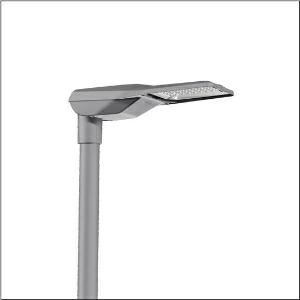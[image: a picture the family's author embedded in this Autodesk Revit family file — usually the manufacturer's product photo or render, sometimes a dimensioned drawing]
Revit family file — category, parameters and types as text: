
# Revit family: streetlight_sl_21_iq_mini___st0_8a_5xe2c41d08gb_f485
name_source: partatom
category: Lighting Fixtures
units: mm (PartAtom-declared; Revit-internal decimal feet)

## family parameters
Cut with Voids When Loaded = No
Host = Face
Light Source = No
Part Type = Normal
Room Calculation Point = No
Round Connector Dimension = Use Diameter
Shared = No

## types (1)
- --- (1 x LED, 5920 lm, 37.1 W, 4000K)
    Apparent Load = 37 VA
    CIE Flux Codes = 38 75 97 100 100
    Color Rendering = 70
    Color Temperature = 4000K
    Default Elevation = 1800 mm
    Description = Streetlight SL 21 iQ mini, mast luminaire, primary light control with lens, of PMMA, primary optical cover: cover, of toughened safety glass, transparent, light distribution: ST0.8a, light emission: direct distribution, primary light characteristic: asymmetric, installation type: post-top, side-entry, LED, High Power LED, rated luminous flux: 5.920lm, luminous efficacy: 160lm/W, light colour: 740, colour temperature: 4000K, control: Auto-Match, Temp-Guard, Lumen-Switch, Night-Set, Smart-Wire, Light-Fading, Desk-Remote (wireless, voltage-free reading and setting of iQ features in the workshop via application-optimized NFC function/RFID function), optimised constant luminous flux control (CLO 2.0), presetting dimming linear, mains connection: 220..240V, AC, 50/60Hz, start of lifetime: 37W, end of service life: 39W, reduction: 18W, luminaire housing, of diecast aluminium, powder-coated, Siteco® metallic grey (DB 702S), corrosivity category C5 mid according to DIN EN ISO 12944, please order mast flange separately, inclination adjustable: 0°, 5°, 10°, 15°, sealing non-destructively replaceable, multi-level sealing system, length: 628mm, width: 235mm, height: 110mm, mast flange for spigot size: 42mm (side-entry): 5XC10008XM4, 60/48mm (side-entry/post-top): 5XC10108XM2, 76/60mm (side-entry/post-top): 5XC10108XM1, protection rating (complete): IP66, insulation class (complete): insulation class II (safety insulation), certification: CE, ENEC, ENEC+, VDE, impact resistance: IK09, permissible operating ambient temperature for outdoor applications: -40..+50°C, standard-compliant lighting for roads and squares, packaging unit: 1 piece

Light Distribution: ST0.8a
    Height = 110 mm
    Lamp = 1 x LED
    Lamp Light Flux = 5920 lm
    Lamp Power = 37.1 W
    Lamp count = 1
    Length = 625 mm
    Luminous efficacy = 160 lm/W
    Manufacturer = Siteco
    ModVariant = No
    Model = 5XE2C41D08GB
    Number of Poles = 1
    OnlyDefault = Yes
    Power Factor = 1
    Product Name = Streetlight SL 21 iQ mini | ST0.8a
    Product group = mast luminaire | pylon top
    ProductGroupID = 6100
    Protection Class = Protection class II
    Protection Degree = IP 66
    RLX_Detail_Level = 1
    RLX_Emergency_Light_Flux = 0 lm
    RLX_Emergency_Type = 0
    RLX_Emergency_Type_DB = No
    RlxData = <blob elided: 91913 chars, md5=da6b27c3>
    Socket = socket
    Standby Power = 0 W
    System Light Flux = 5920 lm
    System Power = 37 W
    Type Comments = factory setting: luminous flux: 100 % | dim-lin: 254 | 385 mA
    Type Image = l_1003519.jpg
    URL = http://relux.com
    VarID = @adj_118911
    Voltage = 0 V
    Weight = 0.00 kg
    Width = 234 mm

## geometry (parser evidence)
native form markers: Blend x4, Sweep x10
no freeform markers — native parametric forms only
